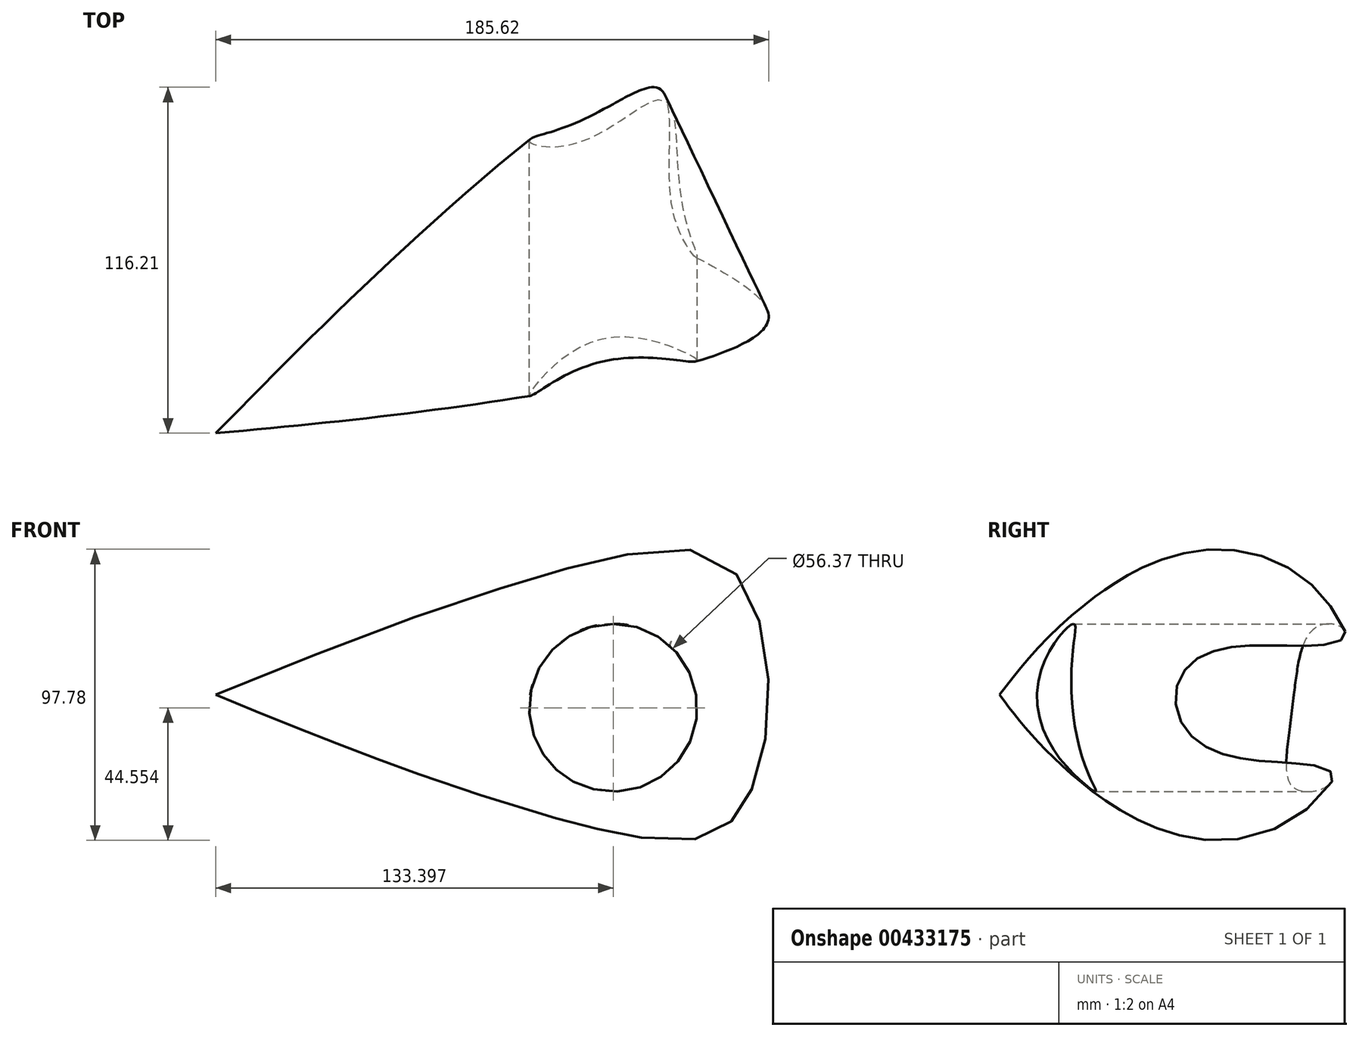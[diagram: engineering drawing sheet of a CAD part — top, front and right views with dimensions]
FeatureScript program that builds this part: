
annotation { "Feature Type Name" : "Feature", "Feature Type Description" : "" }
export const myFeature = defineFeature(function(context is Context, id is Id, definition is map)
    precondition{}
    {
        {
            var Q0;
            Q0=qCreatedBy(makeId("Top.planeOp"),FACE);
            var sketch = newSketch(context, id + "F0", { "sketchPlane" : qUnion([Q0])});
            skFitSpline(sketch, "E0", {"points": [v(41.14, 27.97) * mm, v(44.7, 79.98) * mm, v(-26.27, 33.2) * mm, v(-101.76, -40) * mm], "startDerivative": vector(65.1, 266.28) * mm, "endDerivative": vector(-176.67, -180.18) * mm});
            skLineSegment(sketch, "E1", {"start": v(0, 0) * mm, "end": v(-130.22, -109.27) * mm});
            skLineSegment(sketch, "E2", {"start": v(41.14, 27.97) * mm, "end": v(-101.76, -40) * mm});
            skSolve(sketch);
        }
        {
            var Q0;
            Q0=makeQuery(id+"F0.imprint","IMPRINT",FACE,{"disambiguationData":[TD([[makeQuery(id+"F0.imprint","IMPRINT",EDGE,{"derivedFrom":sQuery(id+"F0.wireOp",EDGE,"E0")}),1.0]])]});
            var Q1;
            Q1=sQuery(id+"F0.wireOp",EDGE,"E2");
            revolve(context, id + "F1", {"entities" : qUnion([Q0]), "axis" : qUnion([Q1]), "revolveType" : RevolveType.FULL});
        }
        {
            var Q0;
            Q0=qCreatedBy(makeId("Front.planeOp"),FACE);
            var sketch = newSketch(context, id + "F2", { "sketchPlane" : qUnion([Q0])});
            skCircle(sketch, "E3", {"center": v(31.64, -4.34) * mm, "radius": 28.19 * mm});
            skSolve(sketch);
        }
        {
            var Q0;
            Q0 = qSketchRegion(id + "F2", true);
            extrude(context, id + "F3", {"entities" : qUnion([Q0]), "operationType" : NewBodyOperationType.REMOVE, "depth" : 74.6 * mm, "hasSecondDirection" : true, "secondDirectionOppositeDirection" : true, "secondDirectionDepth" : 106.8 * mm});
        }
    });
